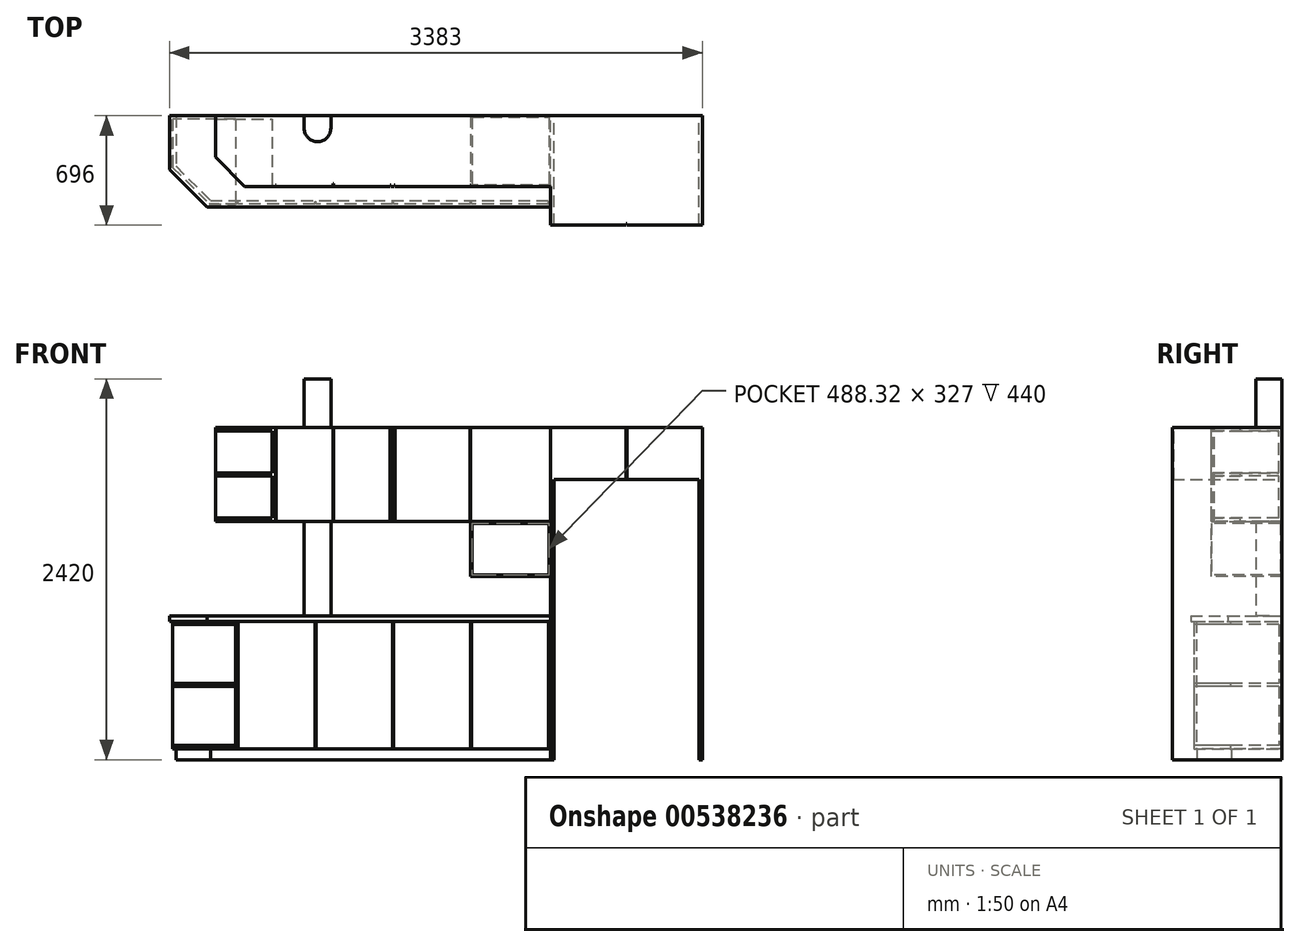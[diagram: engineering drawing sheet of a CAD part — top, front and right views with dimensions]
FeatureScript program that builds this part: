
annotation { "Feature Type Name" : "Feature", "Feature Type Description" : "" }
export const myFeature = defineFeature(function(context is Context, id is Id, definition is map)
    precondition{}
    {
        {
            var Q0;
            Q0=qCreatedBy(makeId("Top.planeOp"),FACE);
            var sketch = newSketch(context, id + "F0", { "sketchPlane" : qUnion([Q0])});
            skLineSegment(sketch, "E0.bottom", {"start": v(0, 0) * mm, "end": v(-2168, 0) * mm});
            skLineSegment(sketch, "E0.top", {"start": v(0, 560) * mm, "end": v(-1800, 560) * mm});
            skLineSegment(sketch, "E0.left", {"start": v(0, 0) * mm, "end": v(0, 560) * mm});
            skLineSegment(sketch, "E1", {"start": v(-2168, 0) * mm, "end": v(-2400, 232) * mm});
            skLineSegment(sketch, "E2", {"start": v(-2400, 232) * mm, "end": v(-2400, 560) * mm});
            skLineSegment(sketch, "E3", {"start": v(-2400, 560) * mm, "end": v(-1800, 560) * mm});
            skSolve(sketch);
        }
        {
            var Q0;
            Q0 = qSketchRegion(id + "F0", true);
            extrude(context, id + "F1", {"entities" : qUnion([Q0]), "depth" : (915 - 35) * mm, "offsetDistance" : 25 * mm});
        }
        {
            var Q0;
            Q0=makeQuery(id+"F1.opExtrude","CAP_FACE",FACE,{"disambiguationData":[OSD([sQuery(id+"F0.wireOp",EDGE,"E0.bottom"),sQuery(id+"F0.wireOp",EDGE,"E0.top"),sQuery(id+"F0.wireOp",EDGE,"E0.left"),sQuery(id+"F0.wireOp",EDGE,"E0.right")])],"isStart":false});
            var sketch = newSketch(context, id + "F2", { "sketchPlane" : qUnion([Q0])});
            skLineSegment(sketch, "E4.bottom", {"start": v(0, 560) * mm, "end": v(0, 560) * mm});
            skLineSegment(sketch, "E4.top", {"start": v(0, -20) * mm, "end": v(0, -20) * mm});
            skLineSegment(sketch, "E4.left", {"start": v(0, 560) * mm, "end": v(0, -20) * mm});
            skLineSegment(sketch, "E4.right", {"start": v(0, 560) * mm, "end": v(0, -20) * mm});
            skLineSegment(sketch, "E5", {"start": v(0, -20) * mm, "end": v(-2182.31, -20) * mm});
            skLineSegment(sketch, "E6", {"start": v(-2182.31, -20) * mm, "end": v(-2420, 217.69) * mm});
            skLineSegment(sketch, "E7", {"start": v(-2420, 217.69) * mm, "end": v(-2420, 560) * mm});
            skLineSegment(sketch, "E8", {"start": v(-2420, 560) * mm, "end": v(0, 560) * mm});
            skSolve(sketch);
        }
        {
            var Q0;
            Q0 = qSketchRegion(id + "F2", true);
            extrude(context, id + "F3", {"entities" : qUnion([Q0]), "depth" : 35 * mm, "offsetDistance" : 25 * mm});
        }
        {
            var Q0;
            Q0=makeQuery(id+"F1.opExtrude","CAP_FACE",FACE,{"disambiguationData":[OSD([sQuery(id+"F0.wireOp",EDGE,"E0.bottom"),sQuery(id+"F0.wireOp",EDGE,"E0.top"),sQuery(id+"F0.wireOp",EDGE,"E0.left"),sQuery(id+"F0.wireOp",EDGE,"E1"),sQuery(id+"F0.wireOp",EDGE,"E2"),sQuery(id+"F0.wireOp",EDGE,"E3")])],"isStart":true});
            var sketch = newSketch(context, id + "F4", { "sketchPlane" : qUnion([Q0])});
            skLineSegment(sketch, "E9", {"start": v(-2380, -560) * mm, "end": v(-2380, -239.9) * mm});
            skLineSegment(sketch, "E10", {"start": v(-2160.1, -20) * mm, "end": v(0, -20) * mm});
            skLineSegment(sketch, "E11", {"start": v(0, -20) * mm, "end": v(0, 0) * mm});
            skLineSegment(sketch, "E12", {"start": v(0, 0) * mm, "end": v(-2168, 0) * mm});
            skLineSegment(sketch, "E13", {"start": v(-2168, 0) * mm, "end": v(-2400, -232) * mm});
            skLineSegment(sketch, "E14", {"start": v(-2400, -232) * mm, "end": v(-2400, -560) * mm});
            skLineSegment(sketch, "E15", {"start": v(-2400, -560) * mm, "end": v(-2380, -560) * mm});
            skLineSegment(sketch, "E16", {"start": v(-2380, -239.9) * mm, "end": v(-2160.1, -20) * mm});
            skSolve(sketch);
        }
        {
            var Q0;
            Q0 = qSketchRegion(id + "F4", true);
            extrude(context, id + "F5", {"entities" : qUnion([Q0]), "operationType" : NewBodyOperationType.REMOVE, "oppositeDirection" : true, "depth" : 70 * mm, "offsetDistance" : 25 * mm});
        }
        {
            var Q0;
            Q0=makeQuery(id+"F1.opExtrude","SWEPT_BODY",BODY,{"disambiguationData":[OSD([sQuery(id+"F0.wireOp",EDGE,"E0.bottom"),sQuery(id+"F0.wireOp",EDGE,"E0.top"),sQuery(id+"F0.wireOp",EDGE,"E0.left"),sQuery(id+"F0.wireOp",EDGE,"E0.right")])]});
            var Q1;
            Q1=makeQuery(id+"F3.opExtrude","SWEPT_BODY",BODY,{"disambiguationData":[OSD([sQuery(id+"F2.wireOp",EDGE,"E4.bottom"),sQuery(id+"F2.wireOp",EDGE,"E4.top"),sQuery(id+"F2.wireOp",EDGE,"E4.left"),sQuery(id+"F2.wireOp",EDGE,"E4.right")])]});
            booleanBodies(context, id + "F6", {"operationType" : BooleanOperationType.UNION, "tools" : qUnion([Q0, Q1])});
        }
        {
            var Q0;
            Q0=qCreatedBy(makeId("Top.planeOp"),FACE);
            var sketch = newSketch(context, id + "F7", { "sketchPlane" : qUnion([Q0])});
            skLineSegment(sketch, "E17.0", {"start": v(0, 20) * mm, "end": v(0, 560) * mm});
            skLineSegment(sketch, "E18.0", {"start": v(0, 0) * mm, "end": v(0, 20) * mm});
            skLineSegment(sketch, "E19", {"start": v(0, 0) * mm, "end": v(0, -20) * mm});
            skLineSegment(sketch, "E20", {"start": v(20, -136) * mm, "end": v(20, 560) * mm});
            skLineSegment(sketch, "E21", {"start": v(20, 560) * mm, "end": v(0, 560) * mm});
            skLineSegment(sketch, "E22", {"start": v(0, -20) * mm, "end": v(0, -136) * mm});
            skLineSegment(sketch, "E23", {"start": v(0, -136) * mm, "end": v(20, -136) * mm});
            skSolve(sketch);
        }
        {
            var Q0;
            Q0 = qSketchRegion(id + "F7", true);
            extrude(context, id + "F8", {"entities" : qUnion([Q0]), "operationType" : NewBodyOperationType.ADD, "depth" : 2110 * mm, "offsetDistance" : 25 * mm});
        }
        {
            var Q0;
            Q0=makeQuery(id+"F8.opExtrude","SWEPT_FACE",FACE,{"disambiguationData":[OSD([sQuery(id+"F7.wireOp",EDGE,"E20")])]});
            var sketch = newSketch(context, id + "F9", { "sketchPlane" : qUnion([Q0])});
            skLineSegment(sketch, "E24.0", {"start": v(-136, 2110) * mm, "end": v(560, 2110) * mm});
            skLineSegment(sketch, "E25", {"start": v(-136, 2110) * mm, "end": v(-136, 1780) * mm});
            skLineSegment(sketch, "E26", {"start": v(-136, 1780) * mm, "end": v(560, 1780) * mm});
            skLineSegment(sketch, "E27", {"start": v(560, 1780) * mm, "end": v(560, 2110) * mm});
            skSolve(sketch);
        }
        {
            var Q0;
            Q0 = qSketchRegion(id + "F9", true);
            extrude(context, id + "F10", {"entities" : qUnion([Q0]), "operationType" : NewBodyOperationType.ADD, "depth" : (903 + 10 + 10) * mm, "offsetDistance" : 25 * mm});
        }
        {
            var Q0;
            Q0=makeQuery(id+"F10.boolean.opBoolean","MERGE",FACE,{"derivedFrom":[makeQuery(id+"F8.opExtrude","CAP_FACE",FACE,{"disambiguationData":[OSD([sQuery(id+"F7.wireOp",EDGE,"E17.0"),sQuery(id+"F7.wireOp",EDGE,"E18.0"),sQuery(id+"F7.wireOp",EDGE,"E19"),sQuery(id+"F7.wireOp",EDGE,"jDNvtvRq-y6cn-oYtA-jtwc-TYGy3E4Eb1i1"),sQuery(id+"F7.wireOp",EDGE,"E20"),sQuery(id+"F7.wireOp",EDGE,"E21")])],"isStart":false}),makeQuery(id+"F10.opExtrude","SWEPT_FACE",FACE,{"disambiguationData":[OSD([sQuery(id+"F9.wireOp",EDGE,"E24.0")])]})]});
            var sketch = newSketch(context, id + "F11", { "sketchPlane" : qUnion([Q0])});
            skLineSegment(sketch, "E28.0", {"start": v(943, -136) * mm, "end": v(943, 560) * mm});
            skLineSegment(sketch, "E29", {"start": v(943, 560) * mm, "end": v(963, 560) * mm});
            skLineSegment(sketch, "E30", {"start": v(943, -136) * mm, "end": v(943, -136) * mm});
            skLineSegment(sketch, "E31", {"start": v(963, 560) * mm, "end": v(963, -136) * mm});
            skLineSegment(sketch, "E32", {"start": v(963, -136) * mm, "end": v(943, -136) * mm});
            skSolve(sketch);
        }
        {
            var Q0;
            Q0 = qSketchRegion(id + "F11", true);
            extrude(context, id + "F12", {"entities" : qUnion([Q0]), "operationType" : NewBodyOperationType.ADD, "oppositeDirection" : true, "depth" : 2110 * mm, "offsetDistance" : 25 * mm});
        }
        {
            var Q0;
            Q0=makeQuery(id+"F12.boolean.opBoolean","MERGE",FACE,{"derivedFrom":[makeQuery(id+"F10.boolean.opBoolean","MERGE",FACE,{"derivedFrom":[makeQuery(id+"F8.opExtrude","CAP_FACE",FACE,{"disambiguationData":[OSD([sQuery(id+"F7.wireOp",EDGE,"E17.0"),sQuery(id+"F7.wireOp",EDGE,"E18.0"),sQuery(id+"F7.wireOp",EDGE,"E19"),sQuery(id+"F7.wireOp",EDGE,"jDNvtvRq-y6cn-oYtA-jtwc-TYGy3E4Eb1i1"),sQuery(id+"F7.wireOp",EDGE,"E20"),sQuery(id+"F7.wireOp",EDGE,"E21")])],"isStart":false}),makeQuery(id+"F10.opExtrude","SWEPT_FACE",FACE,{"disambiguationData":[OSD([sQuery(id+"F9.wireOp",EDGE,"E24.0")])]})]}),makeQuery(id+"F12.opExtrude","CAP_FACE",FACE,{"disambiguationData":[OSD([sQuery(id+"F11.wireOp",EDGE,"E28.0"),sQuery(id+"F11.wireOp",EDGE,"E29"),sQuery(id+"F11.wireOp",EDGE,"wPcqRegp-mC0T-hxdO-CjWI-DLbaqh3OaOpc"),sQuery(id+"F11.wireOp",EDGE,"E30")])],"isStart":true})]});
            var sketch = newSketch(context, id + "F13", { "sketchPlane" : qUnion([Q0])});
            skLineSegment(sketch, "E33", {"start": v(481.5, 751.98) * mm, "end": v(481.5, -258.55) * mm, "construction": true});
            skLineSegment(sketch, "E34", {"start": v(0, 0) * mm, "end": v(0, 705.42) * mm, "construction": true});
            skLineSegment(sketch, "E35", {"start": v(963, -20) * mm, "end": v(963, 710.07) * mm, "construction": true});
            skLineSegment(sketch, "E36.bottom", {"start": v(484, -275.33) * mm, "end": v(479, -275.33) * mm});
            skLineSegment(sketch, "E36.left", {"start": v(484, -275.33) * mm, "end": v(484, -126) * mm});
            skLineSegment(sketch, "E37", {"start": v(479, -275.33) * mm, "end": v(479, -126) * mm});
            skLineSegment(sketch, "E38", {"start": v(479, -126) * mm, "end": v(484, -126) * mm});
            skSolve(sketch);
        }
        {
            var Q0;
            Q0 = qSketchRegion(id + "F13", true);
            extrude(context, id + "F14", {"entities" : qUnion([Q0]), "operationType" : NewBodyOperationType.REMOVE, "endBound" : BoundingType.THROUGH_ALL, "oppositeDirection" : true, "depth" : 25 * mm, "offsetDistance" : 25 * mm});
        }
        {
            var Q0;
            Q0=qCreatedBy(makeId("Top.planeOp"),FACE);
            cPlane(context, id + "F15", {"entities" : qUnion([Q0]), "cplaneType" : CPlaneType.OFFSET, "offset" : 2110 * mm, "width" : 150 * mm, "height" : 150 * mm});
        }
        {
            var Q0;
            Q0=qCreatedBy(id+"F15.planeOp",FACE);
            var sketch = newSketch(context, id + "F16", { "sketchPlane" : qUnion([Q0])});
            skLineSegment(sketch, "E39.0", {"start": v(0, 560) * mm, "end": v(-2420, 560) * mm});
            skLineSegment(sketch, "E40", {"start": v(0, 560) * mm, "end": v(0, 110) * mm});
            skLineSegment(sketch, "E41.0", {"start": v(0, -20) * mm, "end": v(-2182.31, -20) * mm, "construction": true});
            skLineSegment(sketch, "E42", {"start": v(0, 110) * mm, "end": v(-1942.32, 110) * mm});
            skLineSegment(sketch, "E43", {"start": v(-1942.32, 110) * mm, "end": v(-2128.32, 296) * mm});
            skLineSegment(sketch, "E44", {"start": v(-2128.32, 296) * mm, "end": v(-2128.32, 560) * mm});
            skSolve(sketch);
        }
        {
            var Q0;
            Q0 = qSketchRegion(id + "F16", true);
            extrude(context, id + "F17", {"entities" : qUnion([Q0]), "oppositeDirection" : true, "depth" : (2110 - 915 - 600) * mm, "offsetDistance" : 25 * mm});
        }
        {
            var Q0;
            Q0=makeQuery(id+"F1.opExtrude","SWEPT_BODY",BODY,{"disambiguationData":[OSD([sQuery(id+"F0.wireOp",EDGE,"E0.bottom"),sQuery(id+"F0.wireOp",EDGE,"E0.top"),sQuery(id+"F0.wireOp",EDGE,"E0.left"),sQuery(id+"F0.wireOp",EDGE,"E1"),sQuery(id+"F0.wireOp",EDGE,"E2"),sQuery(id+"F0.wireOp",EDGE,"E3")])]});
            var Q1;
            Q1=makeQuery(id+"F17.opExtrude","SWEPT_BODY",BODY,{"disambiguationData":[OSD([sQuery(id+"F16.wireOp",EDGE,"E39.0"),sQuery(id+"F16.wireOp",EDGE,"E40"),sQuery(id+"F16.wireOp",EDGE,"E42"),sQuery(id+"F16.wireOp",EDGE,"E43"),sQuery(id+"F16.wireOp",EDGE,"E44")])]});
            booleanBodies(context, id + "F18", {"operationType" : BooleanOperationType.UNION, "tools" : qUnion([Q0, Q1])});
        }
        {
            var Q0;
            Q0=qCreatedBy(id+"F15.planeOp",FACE);
            cPlane(context, id + "F19", {"entities" : qUnion([Q0]), "cplaneType" : CPlaneType.OFFSET, "offset" : 20 * mm, "oppositeDirection" : true, "width" : 150 * mm, "height" : 150 * mm});
        }
        {
            var Q0;
            Q0=qCreatedBy(id+"F19.planeOp",FACE);
            var sketch = newSketch(context, id + "F20", { "sketchPlane" : qUnion([Q0])});
            skLineSegment(sketch, "E45.0", {"start": v(-1942.32, 110) * mm, "end": v(-2128.32, 296) * mm});
            skLineSegment(sketch, "E46", {"start": v(-1942.32, 110) * mm, "end": v(-1768.32, 110) * mm});
            skLineSegment(sketch, "E47.0", {"start": v(-2128.32, 296) * mm, "end": v(-2128.32, 560) * mm, "construction": true});
            skLineSegment(sketch, "E48", {"start": v(-2128.32, 296) * mm, "end": v(-2128.32, 540) * mm});
            skLineSegment(sketch, "E49", {"start": v(-2128.32, 540) * mm, "end": v(-1768.32, 540) * mm});
            skLineSegment(sketch, "E50", {"start": v(-1768.32, 540) * mm, "end": v(-1768.32, 110) * mm});
            skSolve(sketch);
        }
        {
            var Q0;
            Q0 = qSketchRegion(id + "F20", true);
            extrude(context, id + "F21", {"entities" : qUnion([Q0]), "operationType" : NewBodyOperationType.REMOVE, "oppositeDirection" : true, "depth" : 267.5 * mm, "offsetDistance" : 25 * mm});
        }
        {
            var Q0;
            Q0=qCreatedBy(id+"F19.planeOp",FACE);
            cPlane(context, id + "F22", {"entities" : qUnion([Q0]), "cplaneType" : CPlaneType.OFFSET, "offset" : 287.5 * mm, "oppositeDirection" : true, "width" : 150 * mm, "height" : 150 * mm});
        }
        {
            var Q0;
            Q0=qCreatedBy(id+"F22.planeOp",FACE);
            var sketch = newSketch(context, id + "F23", { "sketchPlane" : qUnion([Q0])});
            skLineSegment(sketch, "E51.0", {"start": v(-2128.32, 540) * mm, "end": v(-1768.32, 540) * mm});
            skLineSegment(sketch, "E52.0", {"start": v(-1768.32, 540) * mm, "end": v(-1768.32, 110) * mm});
            skLineSegment(sketch, "E53.0", {"start": v(-1942.32, 110) * mm, "end": v(-2128.32, 296) * mm});
            skLineSegment(sketch, "E54", {"start": v(-2128.32, 540) * mm, "end": v(-2128.32, 296) * mm});
            skLineSegment(sketch, "E55", {"start": v(-1942.32, 110) * mm, "end": v(-1768.32, 110) * mm});
            skSolve(sketch);
        }
        {
            var Q0;
            Q0 = qSketchRegion(id + "F23", true);
            extrude(context, id + "F24", {"entities" : qUnion([Q0]), "operationType" : NewBodyOperationType.REMOVE, "oppositeDirection" : true, "depth" : 267.5 * mm, "offsetDistance" : 25 * mm});
        }
        {
            var Q0;
            Q0=qCreatedBy(id+"F19.planeOp",FACE);
            var sketch = newSketch(context, id + "F25", { "sketchPlane" : qUnion([Q0])});
            skLineSegment(sketch, "E56.0", {"start": v(0, 110) * mm, "end": v(-1942.32, 110) * mm, "construction": true});
            skLineSegment(sketch, "E57", {"start": v(-1748.32, 110) * mm, "end": v(-1748.32, 360) * mm, "construction": true});
            skLineSegment(sketch, "E58.bottom", {"start": v(-1748.32, 120) * mm, "end": v(-1743.32, 120) * mm});
            skLineSegment(sketch, "E58.top", {"start": v(-1748.32, 93.63) * mm, "end": v(-1743.32, 93.63) * mm});
            skLineSegment(sketch, "E58.left", {"start": v(-1748.32, 120) * mm, "end": v(-1748.32, 93.63) * mm});
            skLineSegment(sketch, "E58.right", {"start": v(-1743.32, 120) * mm, "end": v(-1743.32, 93.63) * mm});
            skLineSegment(sketch, "E59.bottom", {"start": v(-1383.32, 130) * mm, "end": v(-1378.32, 130) * mm});
            skLineSegment(sketch, "E59.top", {"start": v(-1383.32, 99.58) * mm, "end": v(-1378.32, 99.58) * mm});
            skLineSegment(sketch, "E59.left", {"start": v(-1383.32, 130) * mm, "end": v(-1383.32, 99.58) * mm});
            skLineSegment(sketch, "E59.right", {"start": v(-1378.32, 130) * mm, "end": v(-1378.32, 99.58) * mm});
            skLineSegment(sketch, "E60.bottom", {"start": v(-1018.32, 120) * mm, "end": v(-1013.32, 120) * mm});
            skLineSegment(sketch, "E60.top", {"start": v(-1018.32, 93.7) * mm, "end": v(-1013.32, 93.7) * mm});
            skLineSegment(sketch, "E60.left", {"start": v(-1018.32, 120) * mm, "end": v(-1018.32, 93.7) * mm});
            skLineSegment(sketch, "E60.right", {"start": v(-1013.32, 120) * mm, "end": v(-1013.32, 93.7) * mm});
            skLineSegment(sketch, "E61.bottom", {"start": v(-1013.32, 110) * mm, "end": v(-993.32, 110) * mm});
            skLineSegment(sketch, "E61.top", {"start": v(-1013.32, 153.74) * mm, "end": v(-993.32, 153.74) * mm, "construction": true});
            skLineSegment(sketch, "E61.left", {"start": v(-1013.32, 110) * mm, "end": v(-1013.32, 153.74) * mm, "construction": true});
            skLineSegment(sketch, "E61.right", {"start": v(-993.32, 110) * mm, "end": v(-993.32, 153.74) * mm, "construction": true});
            skLineSegment(sketch, "E62.bottom", {"start": v(-993.32, 120) * mm, "end": v(-988.32, 120) * mm});
            skLineSegment(sketch, "E62.top", {"start": v(-993.32, 91.53) * mm, "end": v(-988.32, 91.53) * mm});
            skLineSegment(sketch, "E62.left", {"start": v(-993.32, 120) * mm, "end": v(-993.32, 91.53) * mm});
            skLineSegment(sketch, "E62.right", {"start": v(-988.32, 120) * mm, "end": v(-988.32, 91.53) * mm});
            skLineSegment(sketch, "E63.bottom", {"start": v(-513.32, 120) * mm, "end": v(-508.32, 120) * mm});
            skLineSegment(sketch, "E63.top", {"start": v(-513.32, 90.82) * mm, "end": v(-508.32, 90.82) * mm});
            skLineSegment(sketch, "E63.left", {"start": v(-513.32, 120) * mm, "end": v(-513.32, 90.82) * mm});
            skLineSegment(sketch, "E63.right", {"start": v(-508.32, 120) * mm, "end": v(-508.32, 90.82) * mm});
            skSolve(sketch);
        }
        {
            var Q0;
            Q0 = qSketchRegion(id + "F25", true);
            extrude(context, id + "F26", {"entities" : qUnion([Q0]), "operationType" : NewBodyOperationType.REMOVE, "endBound" : BoundingType.SYMMETRIC, "oppositeDirection" : true, "depth" : 1200 * mm, "offsetDistance" : 25 * mm});
        }
        {
            var Q0;
            Q0=makeQuery(id+"F17.opExtrude","CAP_FACE",FACE,{"disambiguationData":[OSD([sQuery(id+"F16.wireOp",EDGE,"E39.0"),sQuery(id+"F16.wireOp",EDGE,"E40"),sQuery(id+"F16.wireOp",EDGE,"E42"),sQuery(id+"F16.wireOp",EDGE,"E43"),sQuery(id+"F16.wireOp",EDGE,"E44")])],"isStart":false});
            var sketch = newSketch(context, id + "F27", { "sketchPlane" : qUnion([Q0])});
            skLineSegment(sketch, "E64.bottom", {"start": v(-508.32, -110) * mm, "end": v(0, -110) * mm});
            skLineSegment(sketch, "E64.top", {"start": v(-508.32, -560) * mm, "end": v(0, -560) * mm});
            skLineSegment(sketch, "E64.left", {"start": v(-508.32, -110) * mm, "end": v(-508.32, -560) * mm});
            skLineSegment(sketch, "E64.right", {"start": v(0, -110) * mm, "end": v(0, -560) * mm});
            skSolve(sketch);
        }
        {
            var Q0;
            Q0 = qSketchRegion(id + "F27", true);
            extrude(context, id + "F28", {"entities" : qUnion([Q0]), "operationType" : NewBodyOperationType.ADD, "depth" : 350 * mm, "offsetDistance" : 25 * mm});
        }
        {
            var Q0;
            Q0=makeQuery(id+"F28.boolean.opBoolean","MERGE",FACE,{"derivedFrom":[makeQuery(id+"F26.boolean.opBoolean","COPY",FACE,{"derivedFrom":makeQuery(id+"F26.opExtrude","SWEPT_FACE",FACE,{"disambiguationData":[OSD([sQuery(id+"F25.wireOp",EDGE,"E63.right")])]})}),makeQuery(id+"F28.opExtrude","SWEPT_FACE",FACE,{"disambiguationData":[OSD([sQuery(id+"F27.wireOp",EDGE,"E64.left")])]})]});
            var sketch = newSketch(context, id + "F29", { "sketchPlane" : qUnion([Q0])});
            skLineSegment(sketch, "E65.bottom", {"start": v(-120, 1515) * mm, "end": v(-104, 1515) * mm});
            skLineSegment(sketch, "E65.top", {"start": v(-120, 1512) * mm, "end": v(-104, 1512) * mm});
            skLineSegment(sketch, "E65.left", {"start": v(-120, 1515) * mm, "end": v(-120, 1512) * mm});
            skLineSegment(sketch, "E65.right", {"start": v(-104, 1515) * mm, "end": v(-104, 1512) * mm});
            skSolve(sketch);
        }
        {
            var Q0;
            Q0 = qSketchRegion(id + "F29", true);
            extrude(context, id + "F30", {"entities" : qUnion([Q0]), "operationType" : NewBodyOperationType.REMOVE, "oppositeDirection" : true, "depth" : 508.32 * mm, "offsetDistance" : 25 * mm});
        }
        {
            var Q0;
            {var subQ1=makeQuery(id+"F26.opExtrude","SWEPT_FACE",FACE,{"disambiguationData":[OSD([sQuery(id+"F25.wireOp",EDGE,"E63.right")])]});var subQ2=sQuery(id+"F27.wireOp",EDGE,"E64.bottom");var subQ8=sQuery(id+"F29.wireOp",EDGE,"E65.top");var subQ11=sQuery(id+"F16.wireOp",EDGE,"E42");Q0=makeQuery(id+"F30.boolean.opBoolean","SPLIT",FACE,{"disambiguationData":[TD([makeQuery(id+"F30.opExtrude","SWEPT_FACE",FACE,{"disambiguationData":[OSD([subQ8])]})])],"derivedFrom":makeQuery(id+"F28.boolean.opBoolean","MERGE",FACE,{"derivedFrom":[makeQuery(id+"F26.boolean.opBoolean","SPLIT",FACE,{"disambiguationData":[TD([subQ1])],"derivedFrom":makeQuery(id+"F17.opExtrude","SWEPT_FACE",FACE,{"disambiguationData":[OSD([subQ11])]})}),makeQuery(id+"F28.opExtrude","SWEPT_FACE",FACE,{"disambiguationData":[OSD([subQ2])]})]})});}
            var sketch = newSketch(context, id + "F31", { "sketchPlane" : qUnion([Q0])});
            skLineSegment(sketch, "E66.bottom", {"start": v(-498.32, 1502) * mm, "end": v(-10, 1502) * mm});
            skLineSegment(sketch, "E66.top", {"start": v(-498.32, 1175) * mm, "end": v(-10, 1175) * mm});
            skLineSegment(sketch, "E66.left", {"start": v(-498.32, 1502) * mm, "end": v(-498.32, 1175) * mm});
            skLineSegment(sketch, "E66.right", {"start": v(-10, 1502) * mm, "end": v(-10, 1175) * mm});
            skSolve(sketch);
        }
        {
            var Q0;
            Q0 = qSketchRegion(id + "F31", true);
            extrude(context, id + "F32", {"entities" : qUnion([Q0]), "operationType" : NewBodyOperationType.REMOVE, "oppositeDirection" : true, "depth" : 440 * mm, "offsetDistance" : 25 * mm});
        }
        {
            var Q0;
            Q0=makeQuery(id+"F1.opExtrude","SWEPT_FACE",FACE,{"disambiguationData":[OSD([sQuery(id+"F0.wireOp",EDGE,"E2")])]});
            var sketch = newSketch(context, id + "F33", { "sketchPlane" : qUnion([Q0])});
            skLineSegment(sketch, "E67.bottom", {"start": v(-540, 860) * mm, "end": v(20, 860) * mm});
            skLineSegment(sketch, "E67.top", {"start": v(-540, 485) * mm, "end": v(20, 485) * mm});
            skLineSegment(sketch, "E67.left", {"start": v(-540, 860) * mm, "end": v(-540, 485) * mm});
            skLineSegment(sketch, "E67.right", {"start": v(20, 860) * mm, "end": v(20, 485) * mm});
            skLineSegment(sketch, "E68.bottom", {"start": v(-540, 465) * mm, "end": v(20, 465) * mm});
            skLineSegment(sketch, "E68.top", {"start": v(-540, 90) * mm, "end": v(20, 90) * mm});
            skLineSegment(sketch, "E68.left", {"start": v(-540, 465) * mm, "end": v(-540, 90) * mm});
            skLineSegment(sketch, "E68.right", {"start": v(20, 465) * mm, "end": v(20, 90) * mm});
            skSolve(sketch);
        }
        {
            var Q0;
            Q0 = qSketchRegion(id + "F33", true);
            extrude(context, id + "F34", {"entities" : qUnion([Q0]), "operationType" : NewBodyOperationType.REMOVE, "oppositeDirection" : true, "depth" : 400 * mm, "offsetDistance" : 25 * mm});
        }
        {
            var Q0;
            Q0=makeQuery(id+"F8.boolean.opBoolean","MERGE",FACE,{"derivedFrom":[makeQuery(id+"F1.opExtrude","CAP_FACE",FACE,{"disambiguationData":[OSD([sQuery(id+"F0.wireOp",EDGE,"E0.bottom"),sQuery(id+"F0.wireOp",EDGE,"E0.top"),sQuery(id+"F0.wireOp",EDGE,"E0.left"),sQuery(id+"F0.wireOp",EDGE,"E1"),sQuery(id+"F0.wireOp",EDGE,"E2"),sQuery(id+"F0.wireOp",EDGE,"E3")])],"isStart":true}),makeQuery(id+"F8.opExtrude","CAP_FACE",FACE,{"disambiguationData":[OSD([sQuery(id+"F7.wireOp",EDGE,"E17.0"),sQuery(id+"F7.wireOp",EDGE,"E18.0"),sQuery(id+"F7.wireOp",EDGE,"E19"),sQuery(id+"F7.wireOp",EDGE,"E20"),sQuery(id+"F7.wireOp",EDGE,"E21"),sQuery(id+"F7.wireOp",EDGE,"E22"),sQuery(id+"F7.wireOp",EDGE,"E23")])],"isStart":true})]});
            var sketch = newSketch(context, id + "F35", { "sketchPlane" : qUnion([Q0])});
            skLineSegment(sketch, "E69.0", {"start": v(-2000, -540) * mm, "end": v(-2000, 0) * mm, "construction": true});
            skLineSegment(sketch, "E70.bottom", {"start": v(-1990, 4.76) * mm, "end": v(-1985, 4.76) * mm});
            skLineSegment(sketch, "E70.top", {"start": v(-1990, -15) * mm, "end": v(-1985, -15) * mm});
            skLineSegment(sketch, "E70.left", {"start": v(-1990, 4.76) * mm, "end": v(-1990, -15) * mm});
            skLineSegment(sketch, "E70.right", {"start": v(-1985, 4.76) * mm, "end": v(-1985, -15) * mm});
            skLineSegment(sketch, "E71.bottom", {"start": v(-1496.25, 8.96) * mm, "end": v(-1491.25, 8.96) * mm});
            skLineSegment(sketch, "E71.top", {"start": v(-1496.25, -15.1) * mm, "end": v(-1491.25, -15.1) * mm});
            skLineSegment(sketch, "E71.left", {"start": v(-1496.25, 8.96) * mm, "end": v(-1496.25, -15.1) * mm});
            skLineSegment(sketch, "E71.right", {"start": v(-1491.25, 8.96) * mm, "end": v(-1491.25, -15.1) * mm});
            skLineSegment(sketch, "E72.bottom", {"start": v(-1002.5, 7.23) * mm, "end": v(-997.5, 7.23) * mm});
            skLineSegment(sketch, "E72.top", {"start": v(-1002.5, -16.69) * mm, "end": v(-997.5, -16.69) * mm});
            skLineSegment(sketch, "E72.left", {"start": v(-1002.5, 7.23) * mm, "end": v(-1002.5, -16.69) * mm});
            skLineSegment(sketch, "E72.right", {"start": v(-997.5, 7.23) * mm, "end": v(-997.5, -16.69) * mm});
            skLineSegment(sketch, "E73.0", {"start": v(0, 136) * mm, "end": v(0, -20) * mm, "construction": true});
            skLineSegment(sketch, "E74.bottom", {"start": v(-15, 6.9) * mm, "end": v(-10, 6.9) * mm});
            skLineSegment(sketch, "E74.top", {"start": v(-15, -15.82) * mm, "end": v(-10, -15.82) * mm});
            skLineSegment(sketch, "E74.left", {"start": v(-15, 6.9) * mm, "end": v(-15, -15.82) * mm});
            skLineSegment(sketch, "E74.right", {"start": v(-10, 6.9) * mm, "end": v(-10, -15.82) * mm});
            skLineSegment(sketch, "E75.bottom", {"start": v(-508.75, 5.33) * mm, "end": v(-503.75, 5.33) * mm});
            skLineSegment(sketch, "E75.top", {"start": v(-508.75, -16.39) * mm, "end": v(-503.75, -16.39) * mm});
            skLineSegment(sketch, "E75.left", {"start": v(-508.75, 5.33) * mm, "end": v(-508.75, -16.39) * mm});
            skLineSegment(sketch, "E75.right", {"start": v(-503.75, 5.33) * mm, "end": v(-503.75, -16.39) * mm});
            skSolve(sketch);
        }
        {
            var Q0;
            Q0 = qSketchRegion(id + "F35", true);
            extrude(context, id + "F36", {"entities" : qUnion([Q0]), "operationType" : NewBodyOperationType.REMOVE, "oppositeDirection" : true, "depth" : 880 * mm, "offsetDistance" : 25 * mm});
        }
        {
            var Q0;
            Q0=qCreatedBy(makeId("Top.planeOp"),FACE);
            var sketch = newSketch(context, id + "F37", { "sketchPlane" : qUnion([Q0])});
            skLineSegment(sketch, "E76", {"start": v(-2455, 119.14) * mm, "end": v(-2455, 587.1) * mm, "construction": true});
            skLineSegment(sketch, "E77.0", {"start": v(-2420, 217.69) * mm, "end": v(-2420, 560) * mm, "construction": true});
            skLineSegment(sketch, "E78", {"start": v(-2420, 560) * mm, "end": v(-1310.78, 560) * mm, "construction": true});
            skCircle(sketch, "E79", {"center": v(-1480, 480) * mm, "radius": 75 * mm, "construction": true});
            skLineSegment(sketch, "E80", {"start": v(-1555, 560) * mm, "end": v(-1555, 212.1) * mm, "construction": true});
            skLineSegment(sketch, "E81", {"start": v(-1565, 560) * mm, "end": v(-1565, 480) * mm});
            skLineSegment(sketch, "E82", {"start": v(-1395.71, 560) * mm, "end": v(-1395.71, 480) * mm});
            skArc(sketch, "E83", {"start": v(-1565, 480) * mm, "mid": v(-1480.36, 395.36) * mm, "end": v(-1395.71, 480) * mm});
            skLineSegment(sketch, "E84", {"start": v(-1565, 560) * mm, "end": v(-1395.71, 560) * mm});
            skSolve(sketch);
        }
        {
            var Q0;
            Q0 = qSketchRegion(id + "F37", true);
            extrude(context, id + "F38", {"entities" : qUnion([Q0]), "operationType" : NewBodyOperationType.ADD, "depth" : 2420 * mm, "offsetDistance" : 25 * mm});
        }
    });
